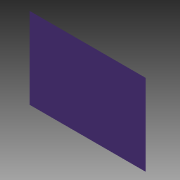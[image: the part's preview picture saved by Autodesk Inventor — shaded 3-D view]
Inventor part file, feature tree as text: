
AUTODESK INVENTOR PART (.ipt)
format: ipt  version: 2018.2 (Build 222227000, 227)  size: 80,896 bytes
history: native  units: mm
features: extrude x1, chamfer x1, sketch x1
ambient origin geometry x8: Origin, YZ Plane, XZ Plane, XY Plane, X Axis, Y Axis, Z Axis, Center Point
bodies: Volumenkörper1 (feature_tree)
feature tree (3):
  extrude  "Extrusion1"  Depth=20.0mm
  chamfer  "Fase1"  Distance=20.0mm
  sketch  "Skizze1"  dims[d0=500.0mm d1=350.0mm d2=20.0mm d3=0.0mm d4=20.0mm d5=2.0mm d6=45.0deg]
